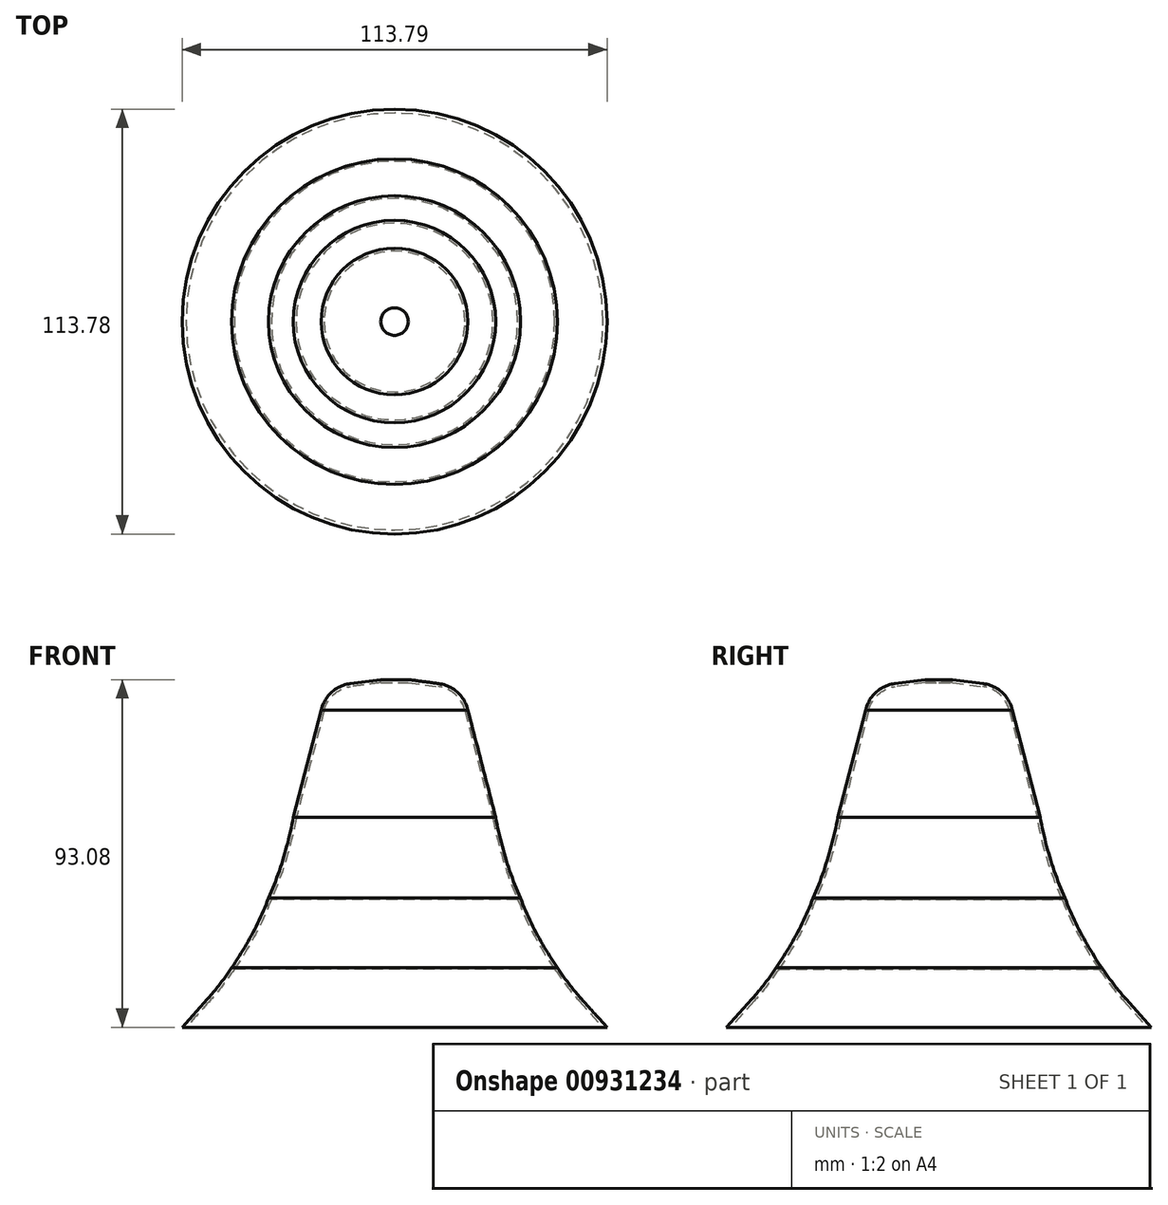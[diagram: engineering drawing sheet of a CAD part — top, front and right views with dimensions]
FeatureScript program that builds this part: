
annotation { "Feature Type Name" : "Feature", "Feature Type Description" : "" }
export const myFeature = defineFeature(function(context is Context, id is Id, definition is map)
    precondition{}
    {
        {
            var Q0;
            Q0=qCreatedBy(makeId("Front.planeOp"),FACE);
            var sketch = newSketch(context, id + "F0", { "sketchPlane" : qUnion([Q0])});
            skLineSegment(sketch, "E0", {"start": v(-175.5, 17.45) * mm, "end": v(-118.6, 17.45) * mm});
            skLineSegment(sketch, "E1", {"start": v(-175.5, 17.45) * mm, "end": v(-168.68, 25.02) * mm});
            skArc(sketch, "E2", {"start": v(-168.68, 25.02) * mm, "mid": v(-165.27, 29.11) * mm, "end": v(-162.18, 33.46) * mm});
            skArc(sketch, "E3", {"start": v(-162.18, 33.46) * mm, "mid": v(-156.7, 42.44) * mm, "end": v(-152.32, 52.01) * mm});
            skArc(sketch, "E4", {"start": v(-152.32, 52.01) * mm, "mid": v(-148.39, 62.64) * mm, "end": v(-145.7, 73.66) * mm});
            skArc(sketch, "E5", {"start": v(-130.45, 109.47) * mm, "mid": v(-135.45, 107.16) * mm, "end": v(-138.24, 102.4) * mm});
            skLineSegment(sketch, "E6", {"start": v(-130.45, 109.47) * mm, "end": v(-122.3, 110.53) * mm});
            skLineSegment(sketch, "E7", {"start": v(-138.24, 102.4) * mm, "end": v(-145.7, 73.66) * mm});
            skLineSegment(sketch, "E8", {"start": v(-118.6, 110.53) * mm, "end": v(-118.6, 17.45) * mm});
            skLineSegment(sketch, "E9", {"start": v(-122.3, 110.53) * mm, "end": v(-118.6, 110.53) * mm});
            skSolve(sketch);
        }
        {
            var Q0;
            Q0=makeQuery(id+"F0.imprint","IMPRINT",FACE,{"disambiguationData":[TD([[makeQuery(id+"F0.imprint","IMPRINT",EDGE,{"derivedFrom":sQuery(id+"F0.wireOp",EDGE,"E0")}),1.0]])]});
            var Q1;
            Q1=sQuery(id+"F0.wireOp",EDGE,"E8");
            var Q2;
            Q2=sQuery(id+"F0.wireOp",EDGE,"E8");
            revolve(context, id + "F1", {"surfaceOperationType" : NewSurfaceOperationType.NEW, "entities" : qUnion([Q0]), "surfaceEntities" : qUnion([Q1]), "axis" : qUnion([Q2]), "revolveType" : RevolveType.FULL});
        }
        {
            var Q0;
            Q0=makeQuery(id+"F1.opRevolve","SWEPT_FACE",FACE,{"disambiguationData":[OSD([sQuery(id+"F0.wireOp",EDGE,"E0")])]});
            shell(context, id + "F2", {"entities" : qUnion([Q0]), "thickness" : 0.8 * mm});
        }
    });
